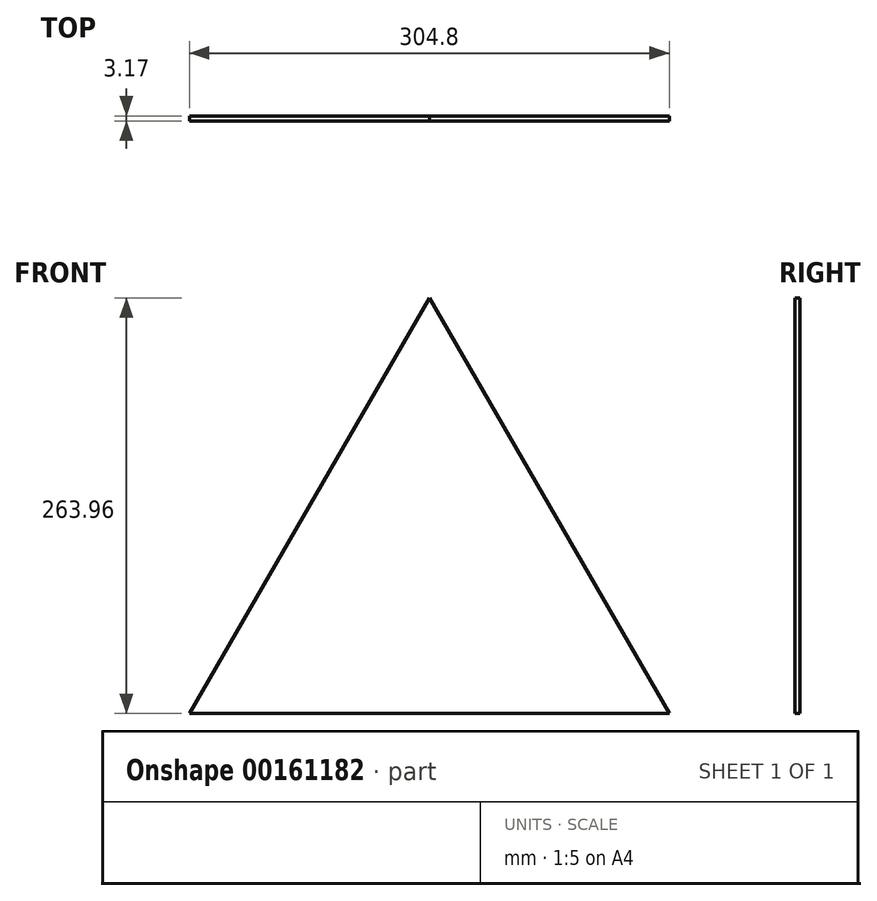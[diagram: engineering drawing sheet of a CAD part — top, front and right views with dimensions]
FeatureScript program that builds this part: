
annotation { "Feature Type Name" : "Feature", "Feature Type Description" : "" }
export const myFeature = defineFeature(function(context is Context, id is Id, definition is map)
    precondition{}
    {
        {
            var Q0;
            Q0=qCreatedBy(makeId("Front.planeOp"),FACE);
            var sketch = newSketch(context, id + "F0", { "sketchPlane" : qUnion([Q0])});
            skLineSegment(sketch, "E0", {"start": v(0, 131.98) * mm, "end": v(152.4, -131.98) * mm});
            skLineSegment(sketch, "E1", {"start": v(152.4, -131.98) * mm, "end": v(-152.4, -131.98) * mm});
            skLineSegment(sketch, "E2", {"start": v(-152.4, -131.98) * mm, "end": v(0, 131.98) * mm});
            skLineSegment(sketch, "E3", {"start": v(0, 131.98) * mm, "end": v(0, -131.98) * mm});
            skSolve(sketch);
        }
        {
            var Q0;
            Q0 = qSketchRegion(id + "F0", true);
            extrude(context, id + "F1", {"entities" : qUnion([Q0]), "depth" : 3.17 * mm});
        }
    });
